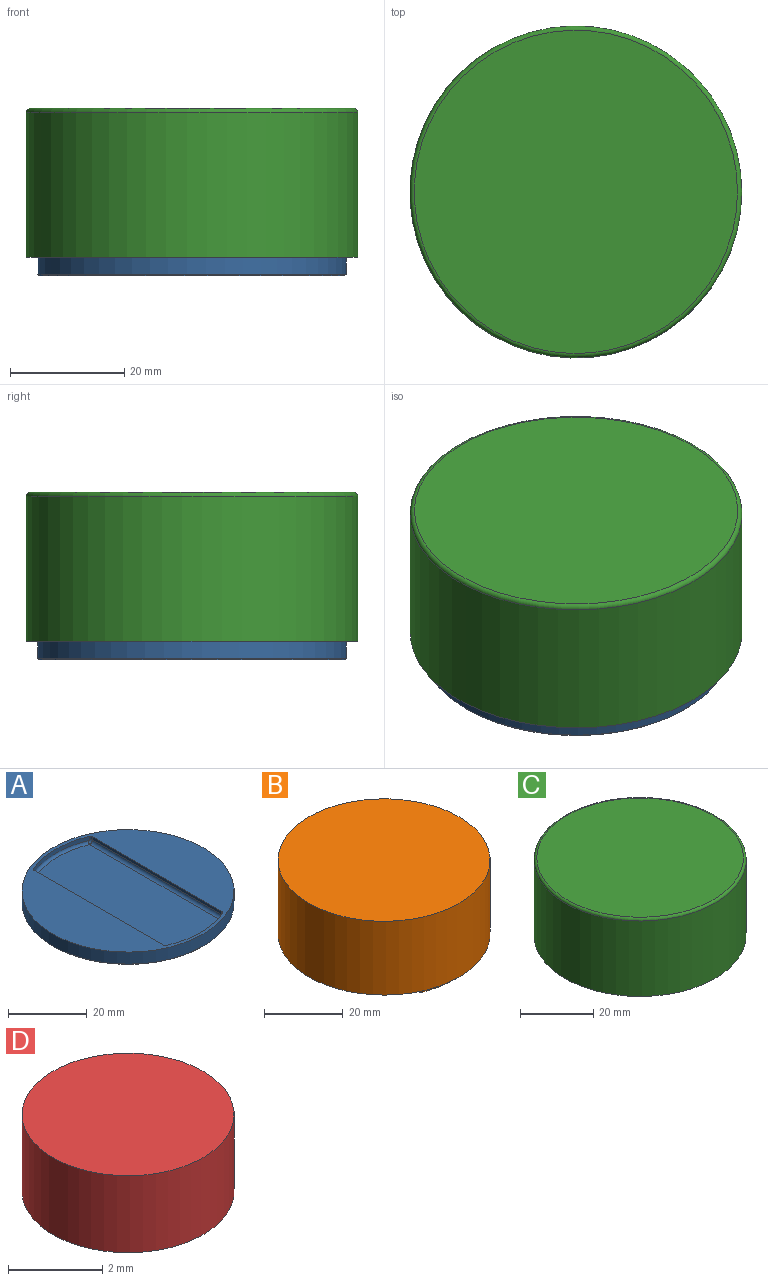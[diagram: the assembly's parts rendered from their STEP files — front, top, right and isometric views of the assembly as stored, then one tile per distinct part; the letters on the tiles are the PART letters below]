
ASSEMBLY  parts=4 mates=3
PART A: 22 faces, bbox 54x56.3x4 mm
  f0: plane 54x54mm, normal (0,0,1), area 1228.8mm2, adj f1,f5,f6,f7,f8,f12,f16,f17
  f1: cylinder r=27mm len=54mm, axis (0,0,-1), area 636.2mm2, adj f0,f3
  f2: cylinder r=26.75mm len=53.5mm, axis (0,0,-1), area 42mm2, adj f3,f4
  f3: plane 54x54mm, normal (0,0,-1), area 42.2mm2, adj f1,f2
  f4: plane 53.5x53.5mm, normal (0,0,-1), area 2248mm2, adj f2
  f5: plane 46.58x1mm, normal (1,0,0), area 46.6mm2, adj f0,f11,f12,f21
  f6: cylinder r=26mm len=20.08mm, axis (0,0,1), area 25.7mm2, adj f0,f17,f18,f19,f20,f21
  f7: plane 46.58x1mm, normal (-1,0,0), area 46.6mm2, adj f0,f10,f16,f17
  f8: cylinder r=26mm len=20.08mm, axis (0,0,1), area 25.7mm2, adj f0,f12,f13,f14,f15,f16
  f9: plane 50.5x19mm, normal (0,0,1), area 936.4mm2, adj f10,f11,f14,f19
  f10: cylinder r=1mm len=46.79mm, axis (0,1,0), area 73.3mm2, adj f7,f9,f15,f18
  f11: cylinder r=1mm len=46.79mm, axis (0,-1,0), area 73.3mm2, adj f5,f9,f13,f20
  f12: cylinder r=0.75mm len=1mm, axis (0,0,1), area 0.9mm2, adj f0,f5,f8,f13
  f13: bspline ~1.25x1.24mm, area 1.1mm2, adj f8,f11,f12,f14
  f14: torus R=25.25mm, axis (0,0,1), area 23.4mm2, adj f8,f9,f13,f15
  f15: bspline ~1.25x1.24mm, area 1.1mm2, adj f8,f10,f14,f16
  f16: cylinder r=0.75mm len=1mm, axis (0,0,1), area 0.9mm2, adj f0,f7,f8,f15
  f17: cylinder r=0.75mm len=1mm, axis (0,0,1), area 0.9mm2, adj f0,f6,f7,f18
  f18: bspline ~1.25x1.24mm, area 1.1mm2, adj f6,f10,f17,f19
  f19: torus R=25.25mm, axis (0,0,1), area 23.4mm2, adj f6,f9,f18,f20
  f20: bspline ~1.25x1.24mm, area 1.1mm2, adj f6,f11,f19,f21
  f21: cylinder r=0.75mm len=1mm, axis (0,0,1), area 0.9mm2, adj f0,f5,f6,f20
PART B: 26 faces, bbox 54x55.2x25 mm
  f0: plane 21x10mm, normal (0,1,0), area 170.4mm2, adj f5,f6,f7,f8,f11,f12,f13,f21
  f1: plane 54x54mm, normal (0,0,-1), area 1233.9mm2, adj f2,f5,f6,f9,f11,f24
  f2: cylinder r=27mm len=54mm, axis (0,0,-1), area 3901.9mm2, adj f1,f3
  f3: plane 54x54mm, normal (0,0,1), area 2290.2mm2, adj f2
  f4: plane 21x10mm, normal (0,-1,0), area 170.4mm2, adj f5,f6,f7,f8,f9,f10,f14,f19
  f5: plane 46.5x2.75mm, normal (-1,0,0), area 127.9mm2, adj f0,f1,f4,f7
  f6: plane 46.5x2.75mm, normal (1,0,0), area 127.9mm2, adj f0,f1,f4,f8
  f7: cylinder r=5.25mm len=46.5mm, axis (0,-1,0), area 511.3mm2, adj f0,f4,f5,f23
  f8: cylinder r=5.25mm len=46.5mm, axis (0,1,0), area 511.3mm2, adj f0,f4,f6,f23
  f9: cylinder r=25.51mm len=21mm, axis (0,0,1), area 21.6mm2, adj f1,f4,f14
  f10: plane 15.52x1.26mm, normal (0,0,-1), area 13.1mm2, adj f4,f14
  f11: cylinder r=25.51mm len=21mm, axis (0,0,1), area 21.6mm2, adj f0,f1,f13
  f12: plane 15.52x1.26mm, normal (0,0,-1), area 13.1mm2, adj f0,f13
  f13: torus R=24.51mm, axis (0,0,-1), area 30.8mm2, adj f0,f11,f12
  f14: torus R=24.51mm, axis (0,0,-1), area 30.8mm2, adj f4,f9,f10
  f15: plane 1.5x1.5mm, normal (0,1,0), area 1.8mm2, adj f22
  f16: plane 1.5x1.5mm, normal (0,1,0), area 1.8mm2, adj f21
  f17: plane 1.5x1.5mm, normal (0,-1,0), area 1.8mm2, adj f20
  f18: plane 1.5x1.5mm, normal (0,-1,0), area 1.8mm2, adj f19
  f19: torus R=0.75mm, axis (0,-1,0), area 13.7mm2, adj f4,f18
  f20: torus R=0.75mm, axis (0,-1,0), area 13.7mm2, adj f4,f17
  f21: torus R=0.75mm, axis (0,1,0), area 13.7mm2, adj f0,f16
  f22: torus R=0.75mm, axis (0,1,0), area 13.7mm2, adj f0,f15
  f23: cylinder r=5.25mm len=46.5mm, axis (0,1,0), area 255.6mm2, adj f0,f4,f7,f8
  f24: cylinder r=2.25mm len=4.5mm, axis (0,0,-1), area 28.3mm2, adj f1,f25
  f25: plane 4.5x4.5mm, normal (0,0,-1), area 15.9mm2, adj f24
PART C: 6 faces, bbox 62.8x62.8x26 mm
  f0: cylinder r=29mm len=58mm, axis (0,0,-1), area 4600.9mm2, adj f2,f3
  f1: plane 56.5x56.5mm, normal (0,0,1), area 2507.2mm2, adj f3
  f2: plane 58x58mm, normal (0,0,-1), area 309.3mm2, adj f0,f4
  f3: torus R=28.25mm, axis (0,0,1), area 212.6mm2, adj f0,f1
  f4: cylinder r=27.25mm len=54.5mm, axis (0,0,-1), area 4066.4mm2, adj f2,f5
  f5: plane 54.5x54.5mm, normal (0,0,-1), area 2332.8mm2, adj f4
PART D: 3 faces, bbox 4.5x4.5x2 mm
  f0: cylinder r=2.25mm len=4.5mm, axis (0,0,-1), area 28.3mm2, adj f1,f2
  f1: plane 4.5x4.5mm, normal (0,0,1), area 15.9mm2, adj f0
  f2: plane 4.5x4.5mm, normal (0,0,-1), area 15.9mm2, adj f0
PLACE A t=(98.45,40.56,-5.87)mm
PLACE B t=(98.45,40.56,-1.87)mm
PLACE C t=(98.45,40.56,-2.62)mm
PLACE D t=(117.2,40.56,-1.87)mm
MATE fastened A.f0 <-> B.f1  axis (0,0,1) through (87.95,40.56,-1.87)mm
MATE revolute C.f4 <-> B.f2  axis (0,0,-1) through (98.45,40.56,21.13)mm
MATE fastened D.f0 <-> B.f24  axis (0,0,-1) through (117.2,40.56,-1.87)mm
